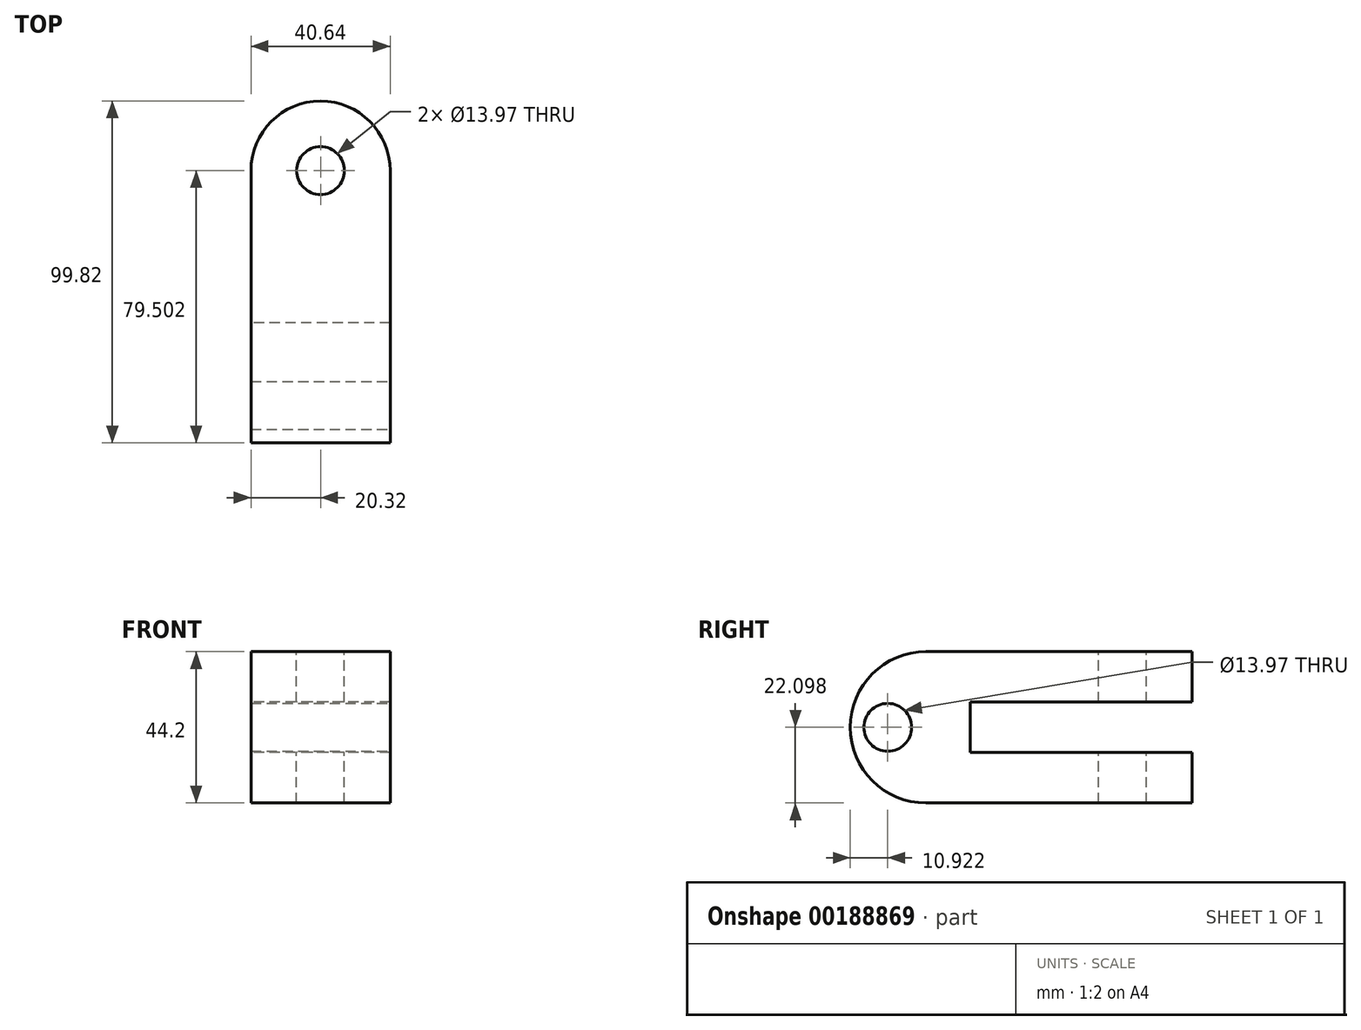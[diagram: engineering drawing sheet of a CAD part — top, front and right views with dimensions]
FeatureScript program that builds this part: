
annotation { "Feature Type Name" : "Feature", "Feature Type Description" : "" }
export const myFeature = defineFeature(function(context is Context, id is Id, definition is map)
    precondition{}
    {
        {
            var Q0;
            Q0=qCreatedBy(makeId("Right.planeOp"),FACE);
            var sketch = newSketch(context, id + "F0", { "sketchPlane" : qUnion([Q0])});
            skLineSegment(sketch, "E0.bottom", {"start": v(0, 0) * mm, "end": v(79.5, 0) * mm});
            skLineSegment(sketch, "E0.top", {"start": v(0, 44.2) * mm, "end": v(79.5, 44.2) * mm});
            skLineSegment(sketch, "E0.left", {"start": v(0, 0) * mm, "end": v(0, 44.2) * mm});
            skLineSegment(sketch, "E0.right", {"start": v(79.5, 0) * mm, "end": v(79.5, 44.2) * mm});
            skSolve(sketch);
        }
        {
            var Q0;
            Q0 = qSketchRegion(id + "F0", true);
            extrude(context, id + "F1", {"entities" : qUnion([Q0]), "depth" : 40.64 * mm});
        }
        {
            var Q0;
            Q0=makeQuery(id+"F1.opExtrude","SWEPT_FACE",FACE,{"disambiguationData":[OSD([sQuery(id+"F0.wireOp",EDGE,"E0.top")])]});
            var sketch = newSketch(context, id + "F2", { "sketchPlane" : qUnion([Q0])});
            skLineSegment(sketch, "E1", {"start": v(20.32, 79.5) * mm, "end": v(20.32, 59.18) * mm});
            skPoint(sketch, "E2", {"position": v(20.32, 59.18) * mm});
            skSolve(sketch);
        }
        {
            var Q0;
            Q0=makeQuery(id+"F1.opExtrude","CAP_FACE",FACE,{"disambiguationData":[OSD([sQuery(id+"F0.wireOp",EDGE,"E0.bottom"),sQuery(id+"F0.wireOp",EDGE,"E0.top"),sQuery(id+"F0.wireOp",EDGE,"E0.left"),sQuery(id+"F0.wireOp",EDGE,"E0.right")])],"isStart":false});
            var Q1;
            Q1=makeQuery(id+"F1.opExtrude","SWEPT_FACE",FACE,{"disambiguationData":[OSD([sQuery(id+"F0.wireOp",EDGE,"E0.right")])]});
            var Q2;
            Q2=makeQuery(id+"F1.opExtrude","CAP_FACE",FACE,{"disambiguationData":[OSD([sQuery(id+"F0.wireOp",EDGE,"E0.bottom"),sQuery(id+"F0.wireOp",EDGE,"E0.top"),sQuery(id+"F0.wireOp",EDGE,"E0.left"),sQuery(id+"F0.wireOp",EDGE,"E0.right")])],"isStart":true});
            shell(context, id + "F3", {"entities" : qUnion([Q0, Q1, Q2]), "thickness" : 14.73 * mm});
        }
        {
            var Q0;
            Q0=sQuery(id+"F2.wireOp",VERTEX,"E2");
            var Q1;
            Q1=makeQuery(id+"F1.opExtrude","SWEPT_BODY",BODY,{"disambiguationData":[OSD([sQuery(id+"F0.wireOp",EDGE,"E0.bottom"),sQuery(id+"F0.wireOp",EDGE,"E0.top"),sQuery(id+"F0.wireOp",EDGE,"E0.left"),sQuery(id+"F0.wireOp",EDGE,"E0.right")])]});
            hole(context, id + "F4", {"style" : HoleStyle.SIMPLE, "endStyle" : HoleEndStyle.THROUGH, "holeDiameter" : 13.97 * mm, "startFromSketch" : true, "locations" : qUnion([Q0]), "scope" : qUnion([Q1]), "isTappedThrough" : true});
        }
        {
            var Q0;
            Q0=makeQuery(id+"F1.opExtrude","CAP_FACE",FACE,{"disambiguationData":[OSD([sQuery(id+"F0.wireOp",EDGE,"E0.bottom"),sQuery(id+"F0.wireOp",EDGE,"E0.top"),sQuery(id+"F0.wireOp",EDGE,"E0.left"),sQuery(id+"F0.wireOp",EDGE,"E0.right")])],"isStart":false});
            var sketch = newSketch(context, id + "F5", { "sketchPlane" : qUnion([Q0])});
            skLineSegment(sketch, "E3", {"start": v(14.73, 29.46) * mm, "end": v(79.5, 29.46) * mm});
            skLineSegment(sketch, "E4", {"start": v(14.73, 22.1) * mm, "end": v(-9.4, 22.1) * mm});
            skPoint(sketch, "E5", {"position": v(-9.4, 22.1) * mm});
            skSolve(sketch);
        }
        {
            var Q0;
            Q0=makeQuery(id+"F1.opExtrude","CAP_FACE",FACE,{"disambiguationData":[OSD([sQuery(id+"F0.wireOp",EDGE,"E0.bottom"),sQuery(id+"F0.wireOp",EDGE,"E0.top"),sQuery(id+"F0.wireOp",EDGE,"E0.left"),sQuery(id+"F0.wireOp",EDGE,"E0.right")])],"isStart":true});
            var sketch = newSketch(context, id + "F6", { "sketchPlane" : qUnion([Q0])});
            skLineSegment(sketch, "E6.bottom", {"start": v(0, 0) * mm, "end": v(20.32, 0) * mm});
            skLineSegment(sketch, "E6.top", {"start": v(0, 44.2) * mm, "end": v(20.32, 44.2) * mm});
            skLineSegment(sketch, "E6.left", {"start": v(0, 0) * mm, "end": v(0, 44.2) * mm});
            skLineSegment(sketch, "E6.right", {"start": v(20.32, 0) * mm, "end": v(20.32, 44.2) * mm});
            skSolve(sketch);
        }
        {
            var Q0;
            Q0 = qSketchRegion(id + "F6", true);
            extrude(context, id + "F7", {"entities" : qUnion([Q0]), "operationType" : NewBodyOperationType.ADD, "oppositeDirection" : true, "depth" : 40.64 * mm});
        }
        {
            var Q0;
            Q0=sQuery(id+"F5.wireOp",VERTEX,"E5");
            var Q1;
            Q1=makeQuery(id+"F1.opExtrude","SWEPT_BODY",BODY,{"disambiguationData":[OSD([sQuery(id+"F0.wireOp",EDGE,"E0.bottom"),sQuery(id+"F0.wireOp",EDGE,"E0.top"),sQuery(id+"F0.wireOp",EDGE,"E0.left"),sQuery(id+"F0.wireOp",EDGE,"E0.right")])]});
            hole(context, id + "F8", {"style" : HoleStyle.SIMPLE, "endStyle" : HoleEndStyle.THROUGH, "holeDiameter" : 13.97 * mm, "startFromSketch" : true, "locations" : qUnion([Q0]), "scope" : qUnion([Q1]), "isTappedThrough" : true});
        }
        {
            var Q0;
            Q0=makeQuery(id+"F7.opExtrude","SWEPT_EDGE",EDGE,{"disambiguationData":[OSD([sQuery(id+"F6.wireOp",EDGE,"E6.top"),sQuery(id+"F6.wireOp",EDGE,"E6.right")])]});
            var Q1;
            Q1=makeQuery(id+"F7.opExtrude","SWEPT_EDGE",EDGE,{"disambiguationData":[OSD([sQuery(id+"F6.wireOp",EDGE,"E6.bottom"),sQuery(id+"F6.wireOp",EDGE,"E6.right")])]});
            fillet(context, id + "F9", {"entities" : qUnion([Q0, Q1]), "radius" : 22.1 * mm, "tangentPropagation" : true, "allowEdgeOverflow" : false});
        }
        {
            var Q0;
            {var subQ0=sQuery(id+"F0.wireOp",EDGE,"E0.right");Q0=makeQuery(id+"F3.opShell","OFFSET_EDGE",EDGE,{"disambiguationData":[OSD([subQ0]),TDD([makeQuery(id+"F1.opExtrude","CAP_EDGE",EDGE,{"disambiguationData":[OSD([subQ0])],"isStart":false})])]});}
            var Q1;
            {var subQ0=sQuery(id+"F0.wireOp",EDGE,"E0.right");Q1=makeQuery(id+"F3.opShell","OFFSET_EDGE",EDGE,{"disambiguationData":[OSD([subQ0]),TDD([makeQuery(id+"F1.opExtrude","CAP_EDGE",EDGE,{"disambiguationData":[OSD([subQ0])],"isStart":true})])]});}
            var Q2;
            Q2=makeQuery(id+"F1.opExtrude","CAP_EDGE",EDGE,{"disambiguationData":[OSD([sQuery(id+"F0.wireOp",EDGE,"E0.right")])],"isStart":true});
            var Q3;
            Q3=makeQuery(id+"F1.opExtrude","CAP_EDGE",EDGE,{"disambiguationData":[OSD([sQuery(id+"F0.wireOp",EDGE,"E0.right")])],"isStart":false});
            fillet(context, id + "F10", {"entities" : qUnion([Q0, Q1, Q2, Q3]), "radius" : 20.32 * mm, "tangentPropagation" : true, "allowEdgeOverflow" : false});
        }
    });
